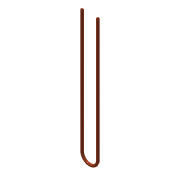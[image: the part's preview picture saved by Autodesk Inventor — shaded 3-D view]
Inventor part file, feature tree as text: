
AUTODESK INVENTOR PART (.ipt)
format: ipt  version: 2016 SP2 (Build 200236200, 236)  size: 104,448 bytes
history: native  units: mm
features: sketch x2, sweep x1
ambient origin geometry x8: Origin, YZ Plane, XZ Plane, XY Plane, X Axis, Y Axis, Z Axis, Center Point
bodies: Body1 (feature_tree)
feature tree (3):
  sweep  "Sweep1"
  sketch  "Sketch1"  dims[d4=6.0mm d5=4.0mm]
  sketch  "Sketch2"  dims[d6=36.0mm d7=280.0mm d8=0.0mm d9=0.0mm d13=280.0mm]
